# Revit family: Shower-Showerhead-KOHLER-Alteo-K-5240
name_source: partatom
category: Plumbing Fixtures
units: mm (PartAtom-declared; Revit-internal decimal feet)

## family parameters
Cut with Voids When Loaded = No
Host = Face
OmniClass Number = 23.31.17.00
OmniClass Title = Showers
Part Type = Normal
Room Calculation Point = No
Round Connector Dimension = Use Diameter
Shared = No

## types (3) — shared parameters
ADA Compliant = No
Assembly Code = D2010700
CW Connection = No
Cold Water Inlet = Cold Water Inlet
Date Modified = 04/03/2023
Default Elevation = 42"
Description = Single-Function Showerhead, 1.75 GPM
Drain Included = No
Flow Rate = 2 GPM
HW Connection = Yes
Height = 5 11/16"
Hot Water Inlet = Hot Water Inlet
Length = 3 15/16"
Manufacturer = Kohler Co.
Master Format 2014 = 22 42 23
Master Format 2014 Name = Residential Showers
Material = Plastic
Pressure = 80.00 psi
Product Documentation Link = https://www.us.kohler.com
Product Name = Alteo
Product Page URL = http://www.us.kohler.com
Tempered Water Inlet = Tempered Water Inlet
URL = https://www.us.kohler.com
Vent Connection = No
Waste Connection = No
Waste Water Outlet = Waste Water Outlet
WaterSense Certified = Yes
Width = 5 11/16"

## per-type parameters (varying)
| type | Finish | Model | Secondary Finish | Type |
| 2BZ-Oil Rubbed Bronze | Kohler-Plastic-2BZ-Oil_Rubbed_Bronze | K-5240-G-2BZ | Kohler-Plastic-2BL-Black | 1 |
| BN-Vibrant Brushed Nickel | KOHLER-Plastic-BN-Vibrant_Brushed_Nickel | K-5240-G-BN | Kohler-Plastic-SR-Vibrant_Bright_Nickel | 2 |
| CP-Polished Chrome | Kohler-Plastic-CP-Polished_Chrome | K-5240-G-CP | Kohler-Plastic-BC-Bright_Chrome | 3 |

## geometry (parser evidence)
native form markers: Sweep x6
no freeform markers — native parametric forms only
